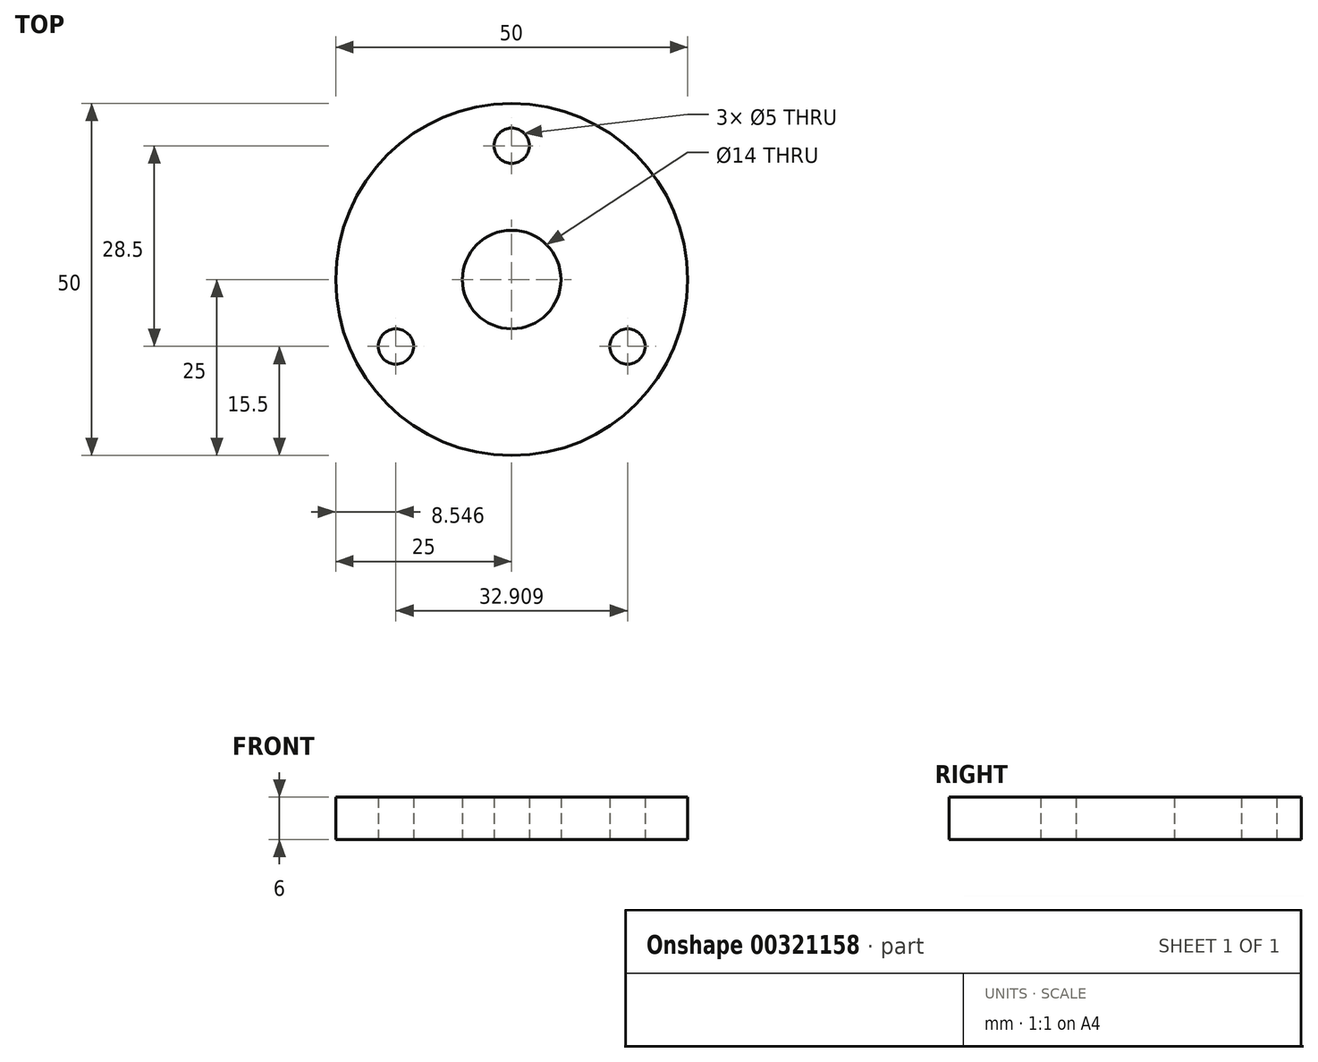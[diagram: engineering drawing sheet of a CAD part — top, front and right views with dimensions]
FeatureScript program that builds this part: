
annotation { "Feature Type Name" : "Feature", "Feature Type Description" : "" }
export const myFeature = defineFeature(function(context is Context, id is Id, definition is map)
    precondition{}
    {
        {
            var Q0;
            Q0=qCreatedBy(makeId("Top.planeOp"),FACE);
            var sketch = newSketch(context, id + "F0", { "sketchPlane" : qUnion([Q0])});
            skCircle(sketch, "E0", {"center": v(0, 0) * mm, "radius": 25 * mm});
            skCircle(sketch, "E1", {"center": v(0, 0) * mm, "radius": 7 * mm});
            skCircle(sketch, "E2", {"center": v(0, 19) * mm, "radius": 2.5 * mm});
            skLineSegment(sketch, "E3", {"start": v(0, 0) * mm, "end": v(-21.65, -12.5) * mm, "construction": true});
            skLineSegment(sketch, "E4", {"start": v(0, 0) * mm, "end": v(21.65, -12.5) * mm, "construction": true});
            skCircle(sketch, "E5.1.0", {"center": v(-16.45, -9.5) * mm, "radius": 2.5 * mm});
            skCircle(sketch, "E5.2.0", {"center": v(16.45, -9.5) * mm, "radius": 2.5 * mm});
            skSolve(sketch);
        }
        {
            var Q0;
            Q0=makeQuery(id+"F0.imprint","IMPRINT",FACE,{"disambiguationData":[TD([[makeQuery(id+"F0.imprint","IMPRINT",EDGE,{"derivedFrom":sQuery(id+"F0.wireOp",EDGE,"E0")}),1.0]])]});
            extrude(context, id + "F1", {"entities" : qUnion([Q0]), "depth" : 6 * mm});
        }
    });
